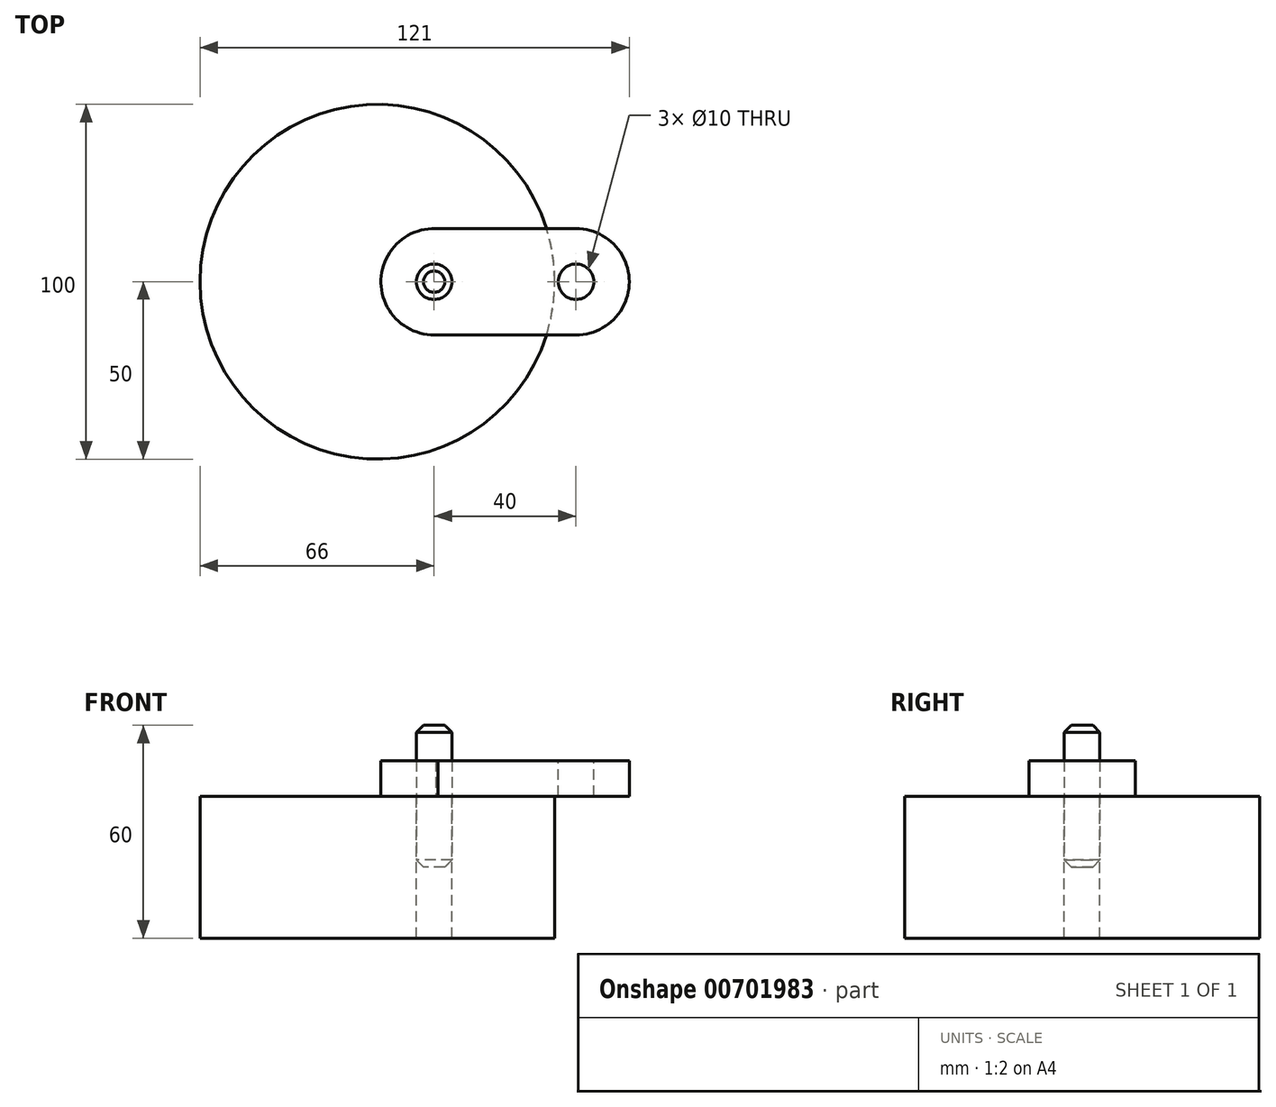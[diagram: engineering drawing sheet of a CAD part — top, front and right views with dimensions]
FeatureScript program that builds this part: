
annotation { "Feature Type Name" : "Feature", "Feature Type Description" : "" }
export const myFeature = defineFeature(function(context is Context, id is Id, definition is map)
    precondition{}
    {
        {
            var Q0;
            Q0=qCreatedBy(makeId("Top.planeOp"),FACE);
            var sketch = newSketch(context, id + "F0", { "sketchPlane" : qUnion([Q0])});
            skCircle(sketch, "E0", {"center": v(0, 0) * mm, "radius": 50 * mm});
            skSolve(sketch);
        }
        {
            var Q0;
            Q0 = qSketchRegion(id + "F0", true);
            extrude(context, id + "F1", {"entities" : qUnion([Q0]), "depth" : 20 * mm, "offsetDistance" : 25 * mm, "hasSecondDirection" : true, "secondDirectionOppositeDirection" : true, "secondDirectionDepth" : 20 * mm});
        }
        {
            var Q0;
            Q0=makeQuery(id+"F1.opExtrude","CAP_FACE",FACE,{"disambiguationData":[OSD([sQuery(id+"F0.wireOp",EDGE,"E0")])],"isStart":false});
            var sketch = newSketch(context, id + "F2", { "sketchPlane" : qUnion([Q0])});
            skCircle(sketch, "E1", {"center": v(16, 0) * mm, "radius": 5 * mm});
            skSolve(sketch);
        }
        {
            var Q0;
            Q0 = qSketchRegion(id + "F2", true);
            extrude(context, id + "F3", {"entities" : qUnion([Q0]), "operationType" : NewBodyOperationType.REMOVE, "endBound" : BoundingType.THROUGH_ALL, "oppositeDirection" : true, "depth" : 25 * mm, "offsetDistance" : 25 * mm});
        }
        {
            var Q0;
            Q0=qCreatedBy(makeId("Top.planeOp"),FACE);
            var sketch = newSketch(context, id + "F4", { "sketchPlane" : qUnion([Q0])});
            skCircle(sketch, "E2.0", {"center": v(16, 0) * mm, "radius": 5 * mm});
            skSolve(sketch);
        }
        {
            var Q0;
            Q0 = qSketchRegion(id + "F4", true);
            extrude(context, id + "F5", {"entities" : qUnion([Q0]), "depth" : 40 * mm, "offsetDistance" : 25 * mm});
        }
        {
            var Q0;
            Q0=makeQuery(id+"F5.opExtrude","CAP_EDGE",EDGE,{"disambiguationData":[OSD([sQuery(id+"F4.wireOp",EDGE,"E2.0")])],"isStart":false});
            var Q1;
            Q1=makeQuery(id+"F5.opExtrude","CAP_EDGE",EDGE,{"disambiguationData":[OSD([sQuery(id+"F4.wireOp",EDGE,"E2.0")])],"isStart":true});
            chamfer(context, id + "F6", {"entities" : qUnion([Q0, Q1]), "width" : 2 * mm, "tangentPropagation" : true});
        }
        {
            var Q0;
            Q0=makeQuery(id+"F1.opExtrude","CAP_FACE",FACE,{"disambiguationData":[OSD([sQuery(id+"F0.wireOp",EDGE,"E0")])],"isStart":false});
            var sketch = newSketch(context, id + "F7", { "sketchPlane" : qUnion([Q0])});
            skCircle(sketch, "E3.0", {"center": v(16, 0) * mm, "radius": 5 * mm});
            skCircle(sketch, "E4.0", {"center": v(16, 0) * mm, "radius": 15 * mm});
            skCircle(sketch, "E5", {"center": v(56, 0) * mm, "radius": 15 * mm});
            skLineSegment(sketch, "E6", {"start": v(16.4, 15) * mm, "end": v(56, 15) * mm});
            skLineSegment(sketch, "E7", {"start": v(14.9, -14.96) * mm, "end": v(55.99, -15) * mm});
            skSolve(sketch);
        }
        {
            var Q0;
            Q0 = qSketchRegion(id + "F7", true);
            extrude(context, id + "F8", {"entities" : qUnion([Q0]), "depth" : 10 * mm, "offsetDistance" : 25 * mm});
        }
        {
            var Q0;
            Q0=makeQuery(id+"F8.opExtrude","CAP_FACE",FACE,{"disambiguationData":[OSD([sQuery(id+"F7.wireOp",EDGE,"E3.0"),sQuery(id+"F7.wireOp",EDGE,"E4.0"),sQuery(id+"F7.wireOp",EDGE,"E5"),sQuery(id+"F7.wireOp",EDGE,"E6"),sQuery(id+"F7.wireOp",EDGE,"E7")])],"isStart":false});
            var sketch = newSketch(context, id + "F9", { "sketchPlane" : qUnion([Q0])});
            skCircle(sketch, "E8", {"center": v(56, 0) * mm, "radius": 5 * mm});
            skSolve(sketch);
        }
        {
            var Q0;
            Q0 = qSketchRegion(id + "F9", true);
            extrude(context, id + "F10", {"entities" : qUnion([Q0]), "operationType" : NewBodyOperationType.REMOVE, "endBound" : BoundingType.THROUGH_ALL, "oppositeDirection" : true, "depth" : 25 * mm, "offsetDistance" : 25 * mm});
        }
    });
